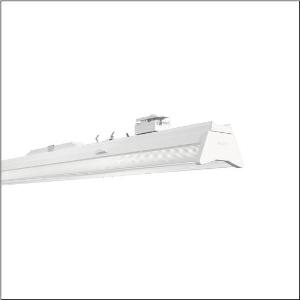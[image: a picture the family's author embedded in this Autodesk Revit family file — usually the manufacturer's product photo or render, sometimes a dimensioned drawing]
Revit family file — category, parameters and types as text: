
# Revit family: licross_r__21_performance_ho_52td16dn4e5m_0710
name_source: partatom
category: Lighting Fixtures
units: mm (PartAtom-declared; Revit-internal decimal feet)

## family parameters
Cut with Voids When Loaded = No
Host = Face
Light Source = No
Part Type = Normal
Room Calculation Point = No
Round Connector Dimension = Use Diameter
Shared = No

## types (1)
- --- (1 x LED, 14870 lm, 84.9 W, 4000K)
    Apparent Load = 85 VA
    CIE Flux Codes = 63 87 95 78 100
    Color Rendering = 80
    Color Temperature = 4000K
    Default Elevation = 1800 mm
    Description = Licross® 21 Performance HO, luminaire insert, of sheet steel, galvanised, coil coated, white, length: 1.500mm, width: 120mm, height: 123mm, LED rated luminous flux: 14.870lm, light colour: 840, control gear: DALI 2, with plug, 5-pole, with phase selection, mains connection: 220..240V, AC, 50/60Hz, rated input power: 85W, halogen-free wiring, primary light control with lens, of plastic, primary optical cover: cover, of PMMA, light emission: direct/indirect distribution, primary light characteristic: symmetric, protection rating (complete): IP54, insulation class (complete): insulation class I (protective earthing), certification: CE, ENEC, VDE, UKCA, protection symbol: D if used in an environment with non-conductive dust loads with corresponding accessories, impact resistance: IK06, permissible ambient temperature for indoor applications: -25..+35°C, corresponds to IFS (International Featured Standards) requirements for safety and quality in the food industry, reducing of maximum allowable ambient temperature of 5°C with ceiling mounting, LABS conformity tested according to VDMA 24364:2018-05, packaging unit: 1 piece
    Height = 114 mm
    Lamp = 1 x LED
    Lamp Light Flux = 14870 lm
    Lamp Power = 84.9 W
    Lamp count = 1
    Length = 1500 mm
    Luminous efficacy = 175 lm/W
    Manufacturer = Siteco
    ModVariant = No
    Model = 52TD16DN4E5M
    Mounting Place = Ceiling
    Mounting Type = Pendant
    Number of Poles = 1
    OnlyDefault = Yes
    Power Factor = 1
    Product Name = Licross® 21 Performance HO
    Product group = luminaire insert
    ProductGroupID = 901
    Protection Class = Protection class I
    Protection Degree = IP 54
    RLX_Detail_Level = 1
    RLX_Emergency_Light_Flux = 0 lm
    RLX_Emergency_Type = 0
    RLX_Emergency_Type_DB = No
    RlxData = <blob elided: 33961 chars, md5=f33f8d3f>
    Socket = socket
    Standby Power = 0 W
    System Light Flux = 14870 lm
    System Power = 85 W
    Type Comments = factory setting: luminous flux: 100 % | dim-lin: 254 | 484 mA
    Type Image = l_1256138.jpg
    URL = http://relux.com
    VarID = @adj_078999
    Voltage = 0 V
    Weight = 0.00 kg
    Width = 120 mm

## geometry (parser evidence)
native form markers: Blend x4, Sweep x12
no freeform markers — native parametric forms only
